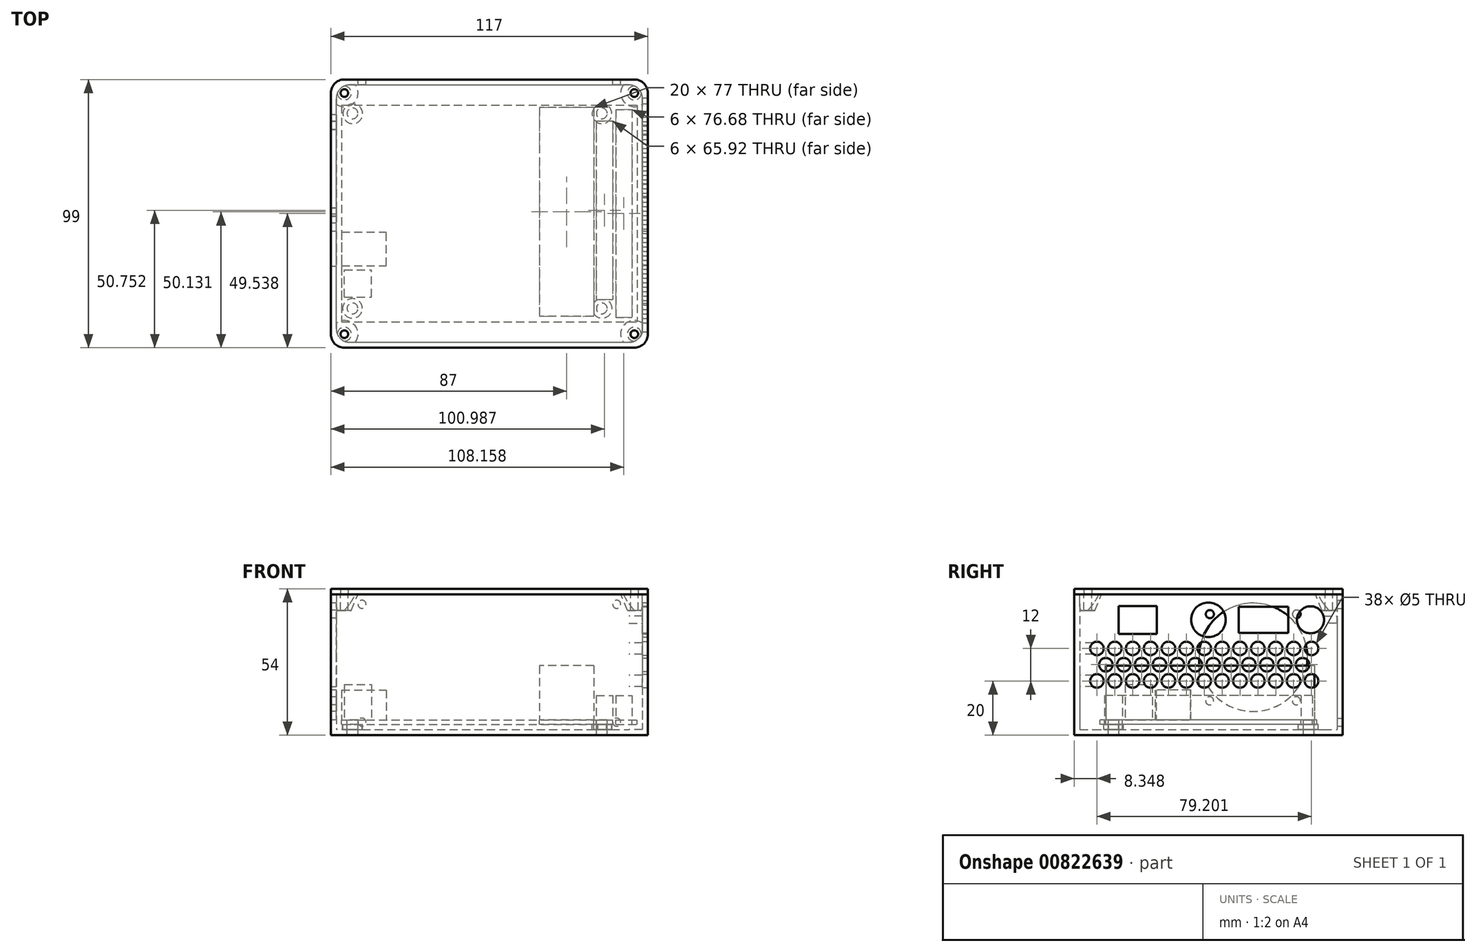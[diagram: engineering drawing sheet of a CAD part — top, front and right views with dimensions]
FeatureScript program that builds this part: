
annotation { "Feature Type Name" : "Feature", "Feature Type Description" : "" }
export const myFeature = defineFeature(function(context is Context, id is Id, definition is map)
    precondition{}
    {
        {
            var Q0;
            Q0=qCreatedBy(makeId("Top.planeOp"),FACE);
            var sketch = newSketch(context, id + "F0", { "sketchPlane" : qUnion([Q0])});
            skLineSegment(sketch, "E0.bottom", {"start": v(-50.5, 37) * mm, "end": v(41.5, 37) * mm, "construction": true});
            skLineSegment(sketch, "E0.top", {"start": v(-50.5, -35) * mm, "end": v(41.5, -35) * mm, "construction": true});
            skLineSegment(sketch, "E0.left", {"start": v(-50.5, 37) * mm, "end": v(-50.5, -35) * mm, "construction": true});
            skLineSegment(sketch, "E0.right", {"start": v(41.5, 37) * mm, "end": v(41.5, -35) * mm, "construction": true});
            skPoint(sketch, "E0.middle", {"position": v(0, 0) * mm});
            skLineSegment(sketch, "E1.bottom", {"start": v(-54.5, 40) * mm, "end": v(54.5, 40) * mm});
            skLineSegment(sketch, "E1.top", {"start": v(-54.5, -40) * mm, "end": v(54.5, -40) * mm});
            skLineSegment(sketch, "E1.left", {"start": v(-54.5, 40) * mm, "end": v(-54.5, -40) * mm});
            skLineSegment(sketch, "E1.right", {"start": v(54.5, 40) * mm, "end": v(54.5, -40) * mm});
            skCircle(sketch, "E2", {"center": v(-50.5, -35) * mm, "radius": 2 * mm});
            skCircle(sketch, "E3", {"center": v(-50.5, 37) * mm, "radius": 2 * mm});
            skCircle(sketch, "E4", {"center": v(41.5, 37) * mm, "radius": 2 * mm});
            skCircle(sketch, "E5", {"center": v(41.5, -35) * mm, "radius": 2 * mm});
            skLineSegment(sketch, "E6.bottom", {"start": v(-53.5, -30.75) * mm, "end": v(-43.5, -30.75) * mm});
            skLineSegment(sketch, "E6.top", {"start": v(-53.5, -20.75) * mm, "end": v(-43.5, -20.75) * mm});
            skLineSegment(sketch, "E6.left", {"start": v(-53.5, -30.75) * mm, "end": v(-53.5, -20.75) * mm});
            skLineSegment(sketch, "E6.right", {"start": v(-43.5, -30.75) * mm, "end": v(-43.5, -20.75) * mm});
            skLineSegment(sketch, "E7.bottom", {"start": v(-54.5, -19.25) * mm, "end": v(-38, -19.25) * mm});
            skLineSegment(sketch, "E7.top", {"start": v(-54.5, -6.75) * mm, "end": v(-38, -6.75) * mm});
            skLineSegment(sketch, "E7.left", {"start": v(-54.5, -19.25) * mm, "end": v(-54.5, -6.75) * mm});
            skLineSegment(sketch, "E7.right", {"start": v(-38, -19.25) * mm, "end": v(-38, -6.75) * mm});
            skLineSegment(sketch, "E8.bottom", {"start": v(38.5, 39.13) * mm, "end": v(18.5, 39.13) * mm});
            skLineSegment(sketch, "E8.top", {"start": v(38.5, -37.87) * mm, "end": v(18.5, -37.87) * mm});
            skLineSegment(sketch, "E8.left", {"start": v(38.5, 39.13) * mm, "end": v(38.5, -37.87) * mm});
            skLineSegment(sketch, "E8.right", {"start": v(18.5, 39.13) * mm, "end": v(18.5, -37.87) * mm});
            skLineSegment(sketch, "E9.bottom", {"start": v(39.49, 34.21) * mm, "end": v(45.49, 34.21) * mm});
            skLineSegment(sketch, "E9.top", {"start": v(39.49, -31.7) * mm, "end": v(45.49, -31.7) * mm});
            skLineSegment(sketch, "E9.left", {"start": v(39.49, 34.21) * mm, "end": v(39.49, -31.7) * mm});
            skLineSegment(sketch, "E9.right", {"start": v(45.49, 34.21) * mm, "end": v(45.49, -31.7) * mm});
            skLineSegment(sketch, "E10.bottom", {"start": v(46.66, 38.38) * mm, "end": v(52.66, 38.38) * mm});
            skLineSegment(sketch, "E10.top", {"start": v(46.66, -38.3) * mm, "end": v(52.66, -38.3) * mm});
            skLineSegment(sketch, "E10.left", {"start": v(46.66, 38.38) * mm, "end": v(46.66, -38.3) * mm});
            skLineSegment(sketch, "E10.right", {"start": v(52.66, 38.38) * mm, "end": v(52.66, -38.3) * mm});
            skSolve(sketch);
        }
        {
            var Q0;
            {var subQ0=sQuery(id+"F0.wireOp",EDGE,"E1.bottom");Q0=makeQuery(id+"F0.imprint","IMPRINT",FACE,{"disambiguationData":[TD([[makeQuery(id+"F0.imprint","IMPRINT",EDGE,{"derivedFrom":subQ0}),-1.0]])]});}
            var Q1;
            Q1=makeQuery(id+"F0.imprint","IMPRINT",FACE,{"disambiguationData":[TD([[makeQuery(id+"F0.imprint","IMPRINT",EDGE,{"derivedFrom":sQuery(id+"F0.wireOp",EDGE,"E7.bottom")}),1.0]])]});
            var Q2;
            Q2=makeQuery(id+"F0.imprint","IMPRINT",FACE,{"disambiguationData":[TD([[makeQuery(id+"F0.imprint","IMPRINT",EDGE,{"derivedFrom":sQuery(id+"F0.wireOp",EDGE,"E6.bottom")}),1.0]])]});
            extrude(context, id + "F1", {"entities" : qUnion([Q0, Q1, Q2]), "oppositeDirection" : true, "depth" : 1.66 * mm, "offsetDistance" : 25 * mm});
        }
        {
            var Q0;
            Q0=makeQuery(id+"F0.imprint","IMPRINT",FACE,{"disambiguationData":[TD([[makeQuery(id+"F0.imprint","IMPRINT",EDGE,{"derivedFrom":sQuery(id+"F0.wireOp",EDGE,"E6.bottom")}),1.0]])]});
            extrude(context, id + "F2", {"entities" : qUnion([Q0]), "operationType" : NewBodyOperationType.ADD, "depth" : 13 * mm, "offsetDistance" : 25 * mm});
        }
        {
            var Q0;
            Q0=makeQuery(id+"F0.imprint","IMPRINT",FACE,{"disambiguationData":[TD([[makeQuery(id+"F0.imprint","IMPRINT",EDGE,{"derivedFrom":sQuery(id+"F0.wireOp",EDGE,"E7.bottom")}),1.0]])]});
            extrude(context, id + "F3", {"entities" : qUnion([Q0]), "operationType" : NewBodyOperationType.ADD, "depth" : 11 * mm, "offsetDistance" : 25 * mm});
        }
        {
            var Q0;
            Q0=makeQuery(id+"F1.opExtrude","CAP_FACE",FACE,{"disambiguationData":[OSD([sQuery(id+"F0.wireOp",EDGE,"E1.bottom"),sQuery(id+"F0.wireOp",EDGE,"E1.top"),sQuery(id+"F0.wireOp",EDGE,"E1.left"),sQuery(id+"F0.wireOp",EDGE,"E1.right"),sQuery(id+"F0.wireOp",EDGE,"E2"),sQuery(id+"F0.wireOp",EDGE,"E3"),sQuery(id+"F0.wireOp",EDGE,"E4"),sQuery(id+"F0.wireOp",EDGE,"E5"),sQuery(id+"F0.wireOp",EDGE,"E7.left")])],"isStart":false});
            var sketch = newSketch(context, id + "F4", { "sketchPlane" : qUnion([Q0])});
            skCircle(sketch, "E11", {"center": v(-50.5, 35) * mm, "radius": 3.62 * mm});
            skCircle(sketch, "E12", {"center": v(41.62, 34.97) * mm, "radius": 3.62 * mm});
            skCircle(sketch, "E13", {"center": v(41.58, -36.84) * mm, "radius": 3.62 * mm});
            skCircle(sketch, "E14", {"center": v(-50.4, -36.84) * mm, "radius": 3.62 * mm});
            skSolve(sketch);
        }
        {
            var Q0;
            Q0=makeQuery(id+"F4.imprint","IMPRINT",FACE,{"disambiguationData":[TD([[makeQuery(id+"F4.imprint","IMPRINT",EDGE,{"derivedFrom":sQuery(id+"F4.wireOp",EDGE,"E11")}),1.0]])]});
            var Q1;
            Q1=makeQuery(id+"F4.imprint","IMPRINT",FACE,{"disambiguationData":[TD([[makeQuery(id+"F4.imprint","IMPRINT",EDGE,{"derivedFrom":sQuery(id+"F4.wireOp",EDGE,"E12")}),1.0]])]});
            var Q2;
            Q2=makeQuery(id+"F4.imprint","IMPRINT",FACE,{"disambiguationData":[TD([[makeQuery(id+"F4.imprint","IMPRINT",EDGE,{"derivedFrom":makeQuery(id+"F1.opExtrude","CAP_EDGE",EDGE,{"disambiguationData":[OSD([sQuery(id+"F0.wireOp",EDGE,"E4")])],"isStart":false})}),1.0]])]});
            var Q3;
            Q3=makeQuery(id+"F4.imprint","IMPRINT",FACE,{"disambiguationData":[TD([[makeQuery(id+"F4.imprint","IMPRINT",EDGE,{"derivedFrom":makeQuery(id+"F1.opExtrude","CAP_EDGE",EDGE,{"disambiguationData":[OSD([sQuery(id+"F0.wireOp",EDGE,"E3")])],"isStart":false})}),1.0]])]});
            var Q4;
            {var subQ0=sQuery(id+"F4.wireOp",EDGE,"E14");var subQ1=makeQuery(id+"F1.opExtrude","CAP_EDGE",EDGE,{"disambiguationData":[OSD([sQuery(id+"F0.wireOp",EDGE,"E1.bottom")])],"isStart":false});var subQ2=makeQuery(id+"F4.imprint","INTERSECT",VERTEX,{"disambiguationData":[OD(0.0)],"derivedFrom":[subQ1,subQ0]});Q4=makeQuery(id+"F4.imprint","IMPRINT",FACE,{"disambiguationData":[TD([[makeQuery(id+"F4.imprint","IMPRINT",EDGE,{"disambiguationData":[TD([[subQ2,-1.0]])],"derivedFrom":subQ0}),1.0]])]});}
            var Q5;
            {var subQ0=sQuery(id+"F4.wireOp",EDGE,"E13");var subQ1=makeQuery(id+"F1.opExtrude","CAP_EDGE",EDGE,{"disambiguationData":[OSD([sQuery(id+"F0.wireOp",EDGE,"E1.bottom")])],"isStart":false});var subQ2=makeQuery(id+"F4.imprint","INTERSECT",VERTEX,{"disambiguationData":[OD(0.0)],"derivedFrom":[subQ1,subQ0]});Q5=makeQuery(id+"F4.imprint","IMPRINT",FACE,{"disambiguationData":[TD([[makeQuery(id+"F4.imprint","IMPRINT",EDGE,{"disambiguationData":[TD([[subQ2,1.0]])],"derivedFrom":subQ0}),1.0]])]});}
            var Q6;
            {var subQ0=sQuery(id+"F4.wireOp",EDGE,"E13");var subQ1=makeQuery(id+"F1.opExtrude","CAP_EDGE",EDGE,{"disambiguationData":[OSD([sQuery(id+"F0.wireOp",EDGE,"E1.bottom")])],"isStart":false});var subQ2=makeQuery(id+"F4.imprint","INTERSECT",VERTEX,{"disambiguationData":[OD(0.0)],"derivedFrom":[subQ1,subQ0]});Q6=makeQuery(id+"F4.imprint","IMPRINT",FACE,{"disambiguationData":[TD([[makeQuery(id+"F4.imprint","IMPRINT",EDGE,{"disambiguationData":[TD([[subQ2,-1.0]])],"derivedFrom":subQ0}),1.0]])]});}
            var Q7;
            {var subQ0=sQuery(id+"F4.wireOp",EDGE,"E13");var subQ1=makeQuery(id+"F1.opExtrude","CAP_EDGE",EDGE,{"disambiguationData":[OSD([sQuery(id+"F0.wireOp",EDGE,"E9.left")])],"isStart":false});var subQ2=makeQuery(id+"F4.imprint","INTERSECT",VERTEX,{"derivedFrom":[subQ1,subQ0]});Q7=makeQuery(id+"F4.imprint","IMPRINT",FACE,{"disambiguationData":[TD([[makeQuery(id+"F4.imprint","IMPRINT",EDGE,{"disambiguationData":[TD([[subQ2,1.0]])],"derivedFrom":subQ0}),1.0]])]});}
            var Q8;
            {var subQ0=sQuery(id+"F4.wireOp",EDGE,"E13");var subQ1=makeQuery(id+"F1.opExtrude","CAP_EDGE",EDGE,{"disambiguationData":[OSD([sQuery(id+"F0.wireOp",EDGE,"E8.left")])],"isStart":false});var subQ2=makeQuery(id+"F4.imprint","INTERSECT",VERTEX,{"disambiguationData":[OD(0.0)],"derivedFrom":[subQ1,subQ0]});Q8=makeQuery(id+"F4.imprint","IMPRINT",FACE,{"disambiguationData":[TD([[makeQuery(id+"F4.imprint","IMPRINT",EDGE,{"disambiguationData":[TD([[subQ2,-1.0]])],"derivedFrom":subQ0}),1.0]])]});}
            var Q9;
            {var subQ0=sQuery(id+"F4.wireOp",EDGE,"E12");var subQ1=makeQuery(id+"F1.opExtrude","CAP_EDGE",EDGE,{"disambiguationData":[OSD([sQuery(id+"F0.wireOp",EDGE,"E8.left")])],"isStart":false});var subQ2=makeQuery(id+"F4.imprint","INTERSECT",VERTEX,{"disambiguationData":[OD(0.0)],"derivedFrom":[subQ1,subQ0]});Q9=makeQuery(id+"F4.imprint","IMPRINT",FACE,{"disambiguationData":[TD([[makeQuery(id+"F4.imprint","IMPRINT",EDGE,{"disambiguationData":[TD([[subQ2,1.0]])],"derivedFrom":subQ0}),1.0]])]});}
            var Q10;
            {var subQ0=sQuery(id+"F4.wireOp",EDGE,"E12");var subQ1=makeQuery(id+"F1.opExtrude","CAP_EDGE",EDGE,{"disambiguationData":[OSD([sQuery(id+"F0.wireOp",EDGE,"E9.top")])],"isStart":false});var subQ2=makeQuery(id+"F4.imprint","INTERSECT",VERTEX,{"disambiguationData":[OD(0.0)],"derivedFrom":[subQ1,subQ0]});Q10=makeQuery(id+"F4.imprint","IMPRINT",FACE,{"disambiguationData":[TD([[makeQuery(id+"F4.imprint","IMPRINT",EDGE,{"disambiguationData":[TD([[subQ2,-1.0]])],"derivedFrom":subQ0}),1.0]])]});}
            var Q11;
            Q11=sQuery(id+"F4.wireOp",EDGE,"E11");
            extrude(context, id + "F5", {"entities" : qUnion([Q0, Q1, Q2, Q3, Q4, Q5, Q6, Q7, Q8, Q9, Q10]), "surfaceEntities" : qUnion([Q11]), "depth" : 2 * mm, "offsetDistance" : 25 * mm});
        }
        {
            var Q0;
            Q0=makeQuery(id+"F5.opExtrude","CAP_FACE",FACE,{"disambiguationData":[OSD([sQuery(id+"F0.wireOp",EDGE,"E2"),sQuery(id+"F4.wireOp",EDGE,"E11")])],"isStart":false});
            var sketch = newSketch(context, id + "F6", { "sketchPlane" : qUnion([Q0])});
            skLineSegment(sketch, "E15.bottom", {"start": v(-56.5, 47.5) * mm, "end": v(56.5, 47.5) * mm});
            skLineSegment(sketch, "E15.top", {"start": v(-56.5, -47.5) * mm, "end": v(56.5, -47.5) * mm});
            skLineSegment(sketch, "E15.left", {"start": v(-56.5, 47.5) * mm, "end": v(-56.5, -47.5) * mm});
            skLineSegment(sketch, "E15.right", {"start": v(56.5, 47.5) * mm, "end": v(56.5, -47.5) * mm});
            skPoint(sketch, "E15.middle", {"position": v(0, 0) * mm});
            skLineSegment(sketch, "E16.bottom", {"start": v(-58.5, 49.5) * mm, "end": v(58.5, 49.5) * mm});
            skLineSegment(sketch, "E16.top", {"start": v(-58.5, -49.5) * mm, "end": v(58.5, -49.5) * mm});
            skLineSegment(sketch, "E16.left", {"start": v(-58.5, 49.5) * mm, "end": v(-58.5, -49.5) * mm});
            skLineSegment(sketch, "E16.right", {"start": v(58.5, 49.5) * mm, "end": v(58.5, -49.5) * mm});
            skCircle(sketch, "E17", {"center": v(-50.5, -37) * mm, "radius": 2 * mm});
            skCircle(sketch, "E18.0.1.0", {"center": v(-50.5, 35) * mm, "radius": 2 * mm});
            skCircle(sketch, "E18.1.0.0", {"center": v(41.5, -37) * mm, "radius": 2 * mm});
            skCircle(sketch, "E18.1.1.0", {"center": v(41.5, 35) * mm, "radius": 2 * mm});
            skLineSegment(sketch, "E18.direction1", {"start": v(-50.5, -37) * mm, "end": v(41.5, -37) * mm, "construction": true});
            skLineSegment(sketch, "E18.direction2", {"start": v(-50.5, -37) * mm, "end": v(-50.5, 35) * mm, "construction": true});
            skSolve(sketch);
        }
        {
            var Q0;
            Q0=makeQuery(id+"F6.imprint","IMPRINT",FACE,{"disambiguationData":[TD([[makeQuery(id+"F6.imprint","IMPRINT",EDGE,{"derivedFrom":sQuery(id+"F6.wireOp",EDGE,"E15.bottom")}),-1.0]])]});
            var Q1;
            Q1=makeQuery(id+"F6.imprint","IMPRINT",FACE,{"disambiguationData":[TD([[makeQuery(id+"F6.imprint","IMPRINT",EDGE,{"derivedFrom":sQuery(id+"F6.wireOp",EDGE,"E15.bottom")}),1.0]])]});
            var Q2;
            Q2=makeQuery(id+"F6.imprint","IMPRINT",FACE,{"disambiguationData":[TD([[makeQuery(id+"F6.imprint","IMPRINT",EDGE,{"derivedFrom":sQuery(id+"F6.wireOp",EDGE,"E18.0.1.0")}),1.0]])]});
            var Q3;
            Q3=sQuery(id+"F6.wireOp",EDGE,"E15.bottom");
            var Q4;
            Q4=sQuery(id+"F6.wireOp",EDGE,"E15.right");
            var Q5;
            Q5=sQuery(id+"F6.wireOp",EDGE,"E15.top");
            var Q6;
            Q6=sQuery(id+"F6.wireOp",EDGE,"E16.left");
            var Q7;
            Q7=sQuery(id+"F6.wireOp",EDGE,"E16.bottom");
            var Q8;
            Q8=sQuery(id+"F6.wireOp",EDGE,"E16.top");
            var Q9;
            Q9=sQuery(id+"F6.wireOp",EDGE,"E16.right");
            extrude(context, id + "F7", {"entities" : qUnion([Q0, Q1, Q2]), "surfaceEntities" : qUnion([Q3, Q4, Q5, Q6, Q7, Q8, Q9]), "depth" : 2 * mm, "offsetDistance" : 25 * mm});
        }
        {
            var Q0;
            Q0=makeQuery(id+"F6.imprint","IMPRINT",FACE,{"disambiguationData":[TD([[makeQuery(id+"F6.imprint","IMPRINT",EDGE,{"derivedFrom":sQuery(id+"F6.wireOp",EDGE,"E15.bottom")}),1.0]])]});
            extrude(context, id + "F8", {"entities" : qUnion([Q0]), "operationType" : NewBodyOperationType.ADD, "oppositeDirection" : true, "depth" : 50 * mm, "offsetDistance" : 25 * mm});
        }
        {
            var Q0;
            {var subQ0=sQuery(id+"F6.wireOp",EDGE,"E16.left");Q0=makeQuery(id+"F8.boolean.opBoolean","MERGE",FACE,{"derivedFrom":[makeQuery(id+"F7.opExtrude","SWEPT_FACE",FACE,{"disambiguationData":[OSD([subQ0])]}),makeQuery(id+"F8.opExtrude","SWEPT_FACE",FACE,{"disambiguationData":[OSD([subQ0])]})]});}
            var sketch = newSketch(context, id + "F9", { "sketchPlane" : qUnion([Q0])});
            skLineSegment(sketch, "E19.bottom", {"start": v(6.53, 0) * mm, "end": v(19.53, 0) * mm});
            skLineSegment(sketch, "E19.top", {"start": v(6.53, 11) * mm, "end": v(19.53, 11) * mm});
            skLineSegment(sketch, "E19.left", {"start": v(6.53, 0) * mm, "end": v(6.53, 11) * mm});
            skLineSegment(sketch, "E19.right", {"start": v(19.53, 0) * mm, "end": v(19.53, 11) * mm});
            skSolve(sketch);
        }
        {
            var Q0;
            Q0 = qSketchRegion(id + "F9", true);
            extrude(context, id + "F10", {"entities" : qUnion([Q0]), "operationType" : NewBodyOperationType.REMOVE, "oppositeDirection" : true, "depth" : 2 * mm, "offsetDistance" : 25 * mm});
        }
        {
            var Q0;
            {var subQ0=sQuery(id+"F6.wireOp",EDGE,"E16.top");Q0=makeQuery(id+"F8.boolean.opBoolean","MERGE",FACE,{"derivedFrom":[makeQuery(id+"F7.opExtrude","SWEPT_FACE",FACE,{"disambiguationData":[OSD([subQ0])]}),makeQuery(id+"F8.opExtrude","SWEPT_FACE",FACE,{"disambiguationData":[OSD([subQ0])]})]});}
            var sketch = newSketch(context, id + "F11", { "sketchPlane" : qUnion([Q0])});
            skLineSegment(sketch, "E20.bottom", {"start": v(-47, -0.86) * mm, "end": v(47, -0.86) * mm, "construction": true});
            skLineSegment(sketch, "E20.top", {"start": v(-47, 42.64) * mm, "end": v(47, 42.64) * mm, "construction": true});
            skLineSegment(sketch, "E20.left", {"start": v(-47, -0.86) * mm, "end": v(-47, 42.64) * mm, "construction": true});
            skLineSegment(sketch, "E20.right", {"start": v(47, -0.86) * mm, "end": v(47, 42.64) * mm, "construction": true});
            skCircle(sketch, "E21", {"center": v(-47, 42.64) * mm, "radius": 1.5 * mm});
            skCircle(sketch, "E22", {"center": v(47, 42.64) * mm, "radius": 1.5 * mm});
            skCircle(sketch, "E23", {"center": v(47, -0.86) * mm, "radius": 1.5 * mm});
            skCircle(sketch, "E24", {"center": v(-47, -0.86) * mm, "radius": 1.5 * mm});
            skSolve(sketch);
        }
        {
            var Q0;
            Q0 = qSketchRegion(id + "F11", true);
            extrude(context, id + "F12", {"entities" : qUnion([Q0]), "operationType" : NewBodyOperationType.REMOVE, "oppositeDirection" : true, "depth" : 2 * mm, "offsetDistance" : 25 * mm});
        }
        {
            var Q0;
            {var subQ0=sQuery(id+"F6.wireOp",EDGE,"E16.right");Q0=makeQuery(id+"F8.boolean.opBoolean","MERGE",FACE,{"derivedFrom":[makeQuery(id+"F7.opExtrude","SWEPT_FACE",FACE,{"disambiguationData":[OSD([subQ0])]}),makeQuery(id+"F8.opExtrude","SWEPT_FACE",FACE,{"disambiguationData":[OSD([subQ0])]})]});}
            var sketch = newSketch(context, id + "F13", { "sketchPlane" : qUnion([Q0])});
            skLineSegment(sketch, "E25.bottom", {"start": v(-33.1, 31.75) * mm, "end": v(-19.1, 31.75) * mm});
            skLineSegment(sketch, "E25.top", {"start": v(-33.1, 42) * mm, "end": v(-19.1, 42) * mm});
            skLineSegment(sketch, "E25.left", {"start": v(-33.1, 31.75) * mm, "end": v(-33.1, 42) * mm});
            skLineSegment(sketch, "E25.right", {"start": v(-19.1, 31.75) * mm, "end": v(-19.1, 42) * mm});
            skCircle(sketch, "E26", {"center": v(-41.15, 26.34) * mm, "radius": 2.5 * mm});
            skCircle(sketch, "E27.1.0.0", {"center": v(-34.55, 26.34) * mm, "radius": 2.5 * mm});
            skCircle(sketch, "E27.2.0.0", {"center": v(-27.95, 26.34) * mm, "radius": 2.5 * mm});
            skCircle(sketch, "E27.3.0.0", {"center": v(-21.35, 26.34) * mm, "radius": 2.5 * mm});
            skCircle(sketch, "E27.4.0.0", {"center": v(-14.75, 26.34) * mm, "radius": 2.5 * mm});
            skCircle(sketch, "E27.5.0.0", {"center": v(-8.15, 26.34) * mm, "radius": 2.5 * mm});
            skCircle(sketch, "E27.6.0.0", {"center": v(-1.55, 26.34) * mm, "radius": 2.5 * mm});
            skCircle(sketch, "E27.7.0.0", {"center": v(5.05, 26.34) * mm, "radius": 2.5 * mm});
            skCircle(sketch, "E27.8.0.0", {"center": v(11.65, 26.34) * mm, "radius": 2.5 * mm});
            skCircle(sketch, "E27.9.0.0", {"center": v(18.25, 26.34) * mm, "radius": 2.5 * mm});
            skCircle(sketch, "E27.10.0.0", {"center": v(24.85, 26.34) * mm, "radius": 2.5 * mm});
            skCircle(sketch, "E27.11.0.0", {"center": v(31.45, 26.34) * mm, "radius": 2.5 * mm});
            skCircle(sketch, "E27.12.0.0", {"center": v(38.05, 26.34) * mm, "radius": 2.5 * mm});
            skLineSegment(sketch, "E27.direction1", {"start": v(-41.15, 26.34) * mm, "end": v(-34.55, 26.34) * mm, "construction": true});
            skCircle(sketch, "E28", {"center": v(-37.85, 20.34) * mm, "radius": 2.5 * mm});
            skPoint(sketch, "E28.centerSnap0", {"position": v(-37.85, 26.34) * mm});
            skCircle(sketch, "E29.1.0.0", {"center": v(-31.25, 20.34) * mm, "radius": 2.5 * mm});
            skCircle(sketch, "E29.2.0.0", {"center": v(-24.65, 20.34) * mm, "radius": 2.5 * mm});
            skCircle(sketch, "E29.3.0.0", {"center": v(-18.05, 20.34) * mm, "radius": 2.5 * mm});
            skCircle(sketch, "E29.4.0.0", {"center": v(-11.45, 20.34) * mm, "radius": 2.5 * mm});
            skCircle(sketch, "E29.5.0.0", {"center": v(-4.85, 20.34) * mm, "radius": 2.5 * mm});
            skCircle(sketch, "E29.6.0.0", {"center": v(1.75, 20.34) * mm, "radius": 2.5 * mm});
            skCircle(sketch, "E29.7.0.0", {"center": v(8.35, 20.34) * mm, "radius": 2.5 * mm});
            skCircle(sketch, "E29.8.0.0", {"center": v(14.95, 20.34) * mm, "radius": 2.5 * mm});
            skCircle(sketch, "E29.9.0.0", {"center": v(21.55, 20.34) * mm, "radius": 2.5 * mm});
            skCircle(sketch, "E29.10.0.0", {"center": v(28.15, 20.34) * mm, "radius": 2.5 * mm});
            skCircle(sketch, "E29.11.0.0", {"center": v(34.75, 20.34) * mm, "radius": 2.5 * mm});
            skLineSegment(sketch, "E29.direction1", {"start": v(-37.85, 20.34) * mm, "end": v(-31.25, 20.34) * mm, "construction": true});
            skCircle(sketch, "E30.1.0.0", {"center": v(-27.95, 14.34) * mm, "radius": 2.5 * mm});
            skPoint(sketch, "E30.1.0.1", {"position": v(-37.85, 14.34) * mm});
            skCircle(sketch, "E30.1.0.2", {"center": v(-8.15, 14.34) * mm, "radius": 2.5 * mm});
            skCircle(sketch, "E30.1.0.3", {"center": v(-1.55, 14.34) * mm, "radius": 2.5 * mm});
            skCircle(sketch, "E30.1.0.4", {"center": v(-21.35, 14.34) * mm, "radius": 2.5 * mm});
            skCircle(sketch, "E30.1.0.5", {"center": v(-14.75, 14.34) * mm, "radius": 2.5 * mm});
            skCircle(sketch, "E30.1.0.6", {"center": v(5.05, 14.34) * mm, "radius": 2.5 * mm});
            skCircle(sketch, "E30.1.0.7", {"center": v(11.65, 14.34) * mm, "radius": 2.5 * mm});
            skLineSegment(sketch, "E30.1.0.8", {"start": v(-41.15, 14.34) * mm, "end": v(-34.55, 14.34) * mm, "construction": true});
            skCircle(sketch, "E30.1.0.9", {"center": v(38.05, 14.34) * mm, "radius": 2.5 * mm});
            skCircle(sketch, "E30.1.0.10", {"center": v(18.25, 14.34) * mm, "radius": 2.5 * mm});
            skCircle(sketch, "E30.1.0.11", {"center": v(24.85, 14.34) * mm, "radius": 2.5 * mm});
            skCircle(sketch, "E30.1.0.12", {"center": v(31.45, 14.34) * mm, "radius": 2.5 * mm});
            skCircle(sketch, "E30.1.0.13", {"center": v(-41.15, 14.34) * mm, "radius": 2.5 * mm});
            skCircle(sketch, "E30.1.0.14", {"center": v(-34.55, 14.34) * mm, "radius": 2.5 * mm});
            skLineSegment(sketch, "E30.direction1", {"start": v(-41.15, 26.34) * mm, "end": v(-41.15, 14.34) * mm, "construction": true});
            skLineSegment(sketch, "E31.direction1", {"start": v(-37.85, 20.34) * mm, "end": v(-37.96, 8.34) * mm, "construction": true});
            skCircle(sketch, "E32", {"center": v(0, 36.91) * mm, "radius": 6.38 * mm});
            skPoint(sketch, "E32.centerSnap0", {"position": v(-19.1, 36.88) * mm});
            skCircle(sketch, "E33", {"center": v(37.68, 36.91) * mm, "radius": 5 * mm});
            skLineSegment(sketch, "E34.bottom", {"start": v(29.44, 41.75) * mm, "end": v(11.13, 41.75) * mm});
            skLineSegment(sketch, "E34.top", {"start": v(29.44, 32.08) * mm, "end": v(11.13, 32.08) * mm});
            skLineSegment(sketch, "E34.left", {"start": v(29.44, 41.75) * mm, "end": v(29.44, 32.08) * mm});
            skLineSegment(sketch, "E34.right", {"start": v(11.13, 41.75) * mm, "end": v(11.13, 32.08) * mm});
            skPoint(sketch, "E34.middle", {"position": v(20.28, 36.91) * mm});
            skLineSegment(sketch, "E35", {"start": v(37.68, 36.91) * mm, "end": v(-34.66, 36.91) * mm, "construction": true});
            skSolve(sketch);
        }
        {
            var Q0;
            Q0=makeQuery(id+"F13.imprint","IMPRINT",FACE,{"disambiguationData":[TD([[makeQuery(id+"F13.imprint","IMPRINT",EDGE,{"derivedFrom":sQuery(id+"F13.wireOp",EDGE,"E25.bottom")}),1.0]])]});
            var Q1;
            Q1=makeQuery(id+"F13.imprint","IMPRINT",FACE,{"disambiguationData":[TD([[makeQuery(id+"F13.imprint","IMPRINT",EDGE,{"derivedFrom":sQuery(id+"F13.wireOp",EDGE,"E32")}),1.0]])]});
            var Q2;
            Q2=makeQuery(id+"F13.imprint","IMPRINT",FACE,{"disambiguationData":[TD([[makeQuery(id+"F13.imprint","IMPRINT",EDGE,{"derivedFrom":sQuery(id+"F13.wireOp",EDGE,"E34.bottom")}),1.0]])]});
            var Q3;
            Q3=makeQuery(id+"F13.imprint","IMPRINT",FACE,{"disambiguationData":[TD([[makeQuery(id+"F13.imprint","IMPRINT",EDGE,{"derivedFrom":sQuery(id+"F13.wireOp",EDGE,"E33")}),1.0]])]});
            var Q4;
            Q4=makeQuery(id+"F8.opExtrude","SWEPT_FACE",FACE,{"disambiguationData":[OSD([sQuery(id+"F6.wireOp",EDGE,"E15.right")])]});
            extrude(context, id + "F14", {"entities" : qUnion([Q0, Q1, Q2, Q3]), "operationType" : NewBodyOperationType.REMOVE, "endBound" : BoundingType.UP_TO_SURFACE, "oppositeDirection" : true, "depth" : 2.5 * mm, "endBoundEntityFace" : qUnion([Q4]), "offsetDistance" : 25 * mm});
        }
        {
            var Q0;
            Q0=makeQuery(id+"F9.imprint","IMPRINT",FACE,{"disambiguationData":[TD([[makeQuery(id+"F9.imprint","IMPRINT",EDGE,{"derivedFrom":sQuery(id+"F9.wireOp",EDGE,"E19.bottom")}),-1.0]])]});
            var sketch = newSketch(context, id + "F15", { "sketchPlane" : qUnion([Q0])});
            skLineSegment(sketch, "E36.bottom", {"start": v(-36.53, 43.01) * mm, "end": v(3.47, 43.01) * mm, "construction": true});
            skLineSegment(sketch, "E36.top", {"start": v(-36.53, 3.16) * mm, "end": v(3.47, 3.16) * mm, "construction": true});
            skLineSegment(sketch, "E36.left", {"start": v(-36.53, 43) * mm, "end": v(-36.53, 3.16) * mm, "construction": true});
            skLineSegment(sketch, "E36.right", {"start": v(3.47, 43) * mm, "end": v(3.47, 3.16) * mm, "construction": true});
            skArc(sketch, "E37", {"start": v(3.47, 23.09) * mm, "mid": v(-35.69, 28.83) * mm, "end": v(0.17, 12.08) * mm});
            skPoint(sketch, "E37.centerSnap0", {"position": v(-36.53, 23.08) * mm});
            skPoint(sketch, "E37.centerSnap1", {"position": v(-16.53, 43.01) * mm});
            skLineSegment(sketch, "E38.bottom", {"start": v(3.47, 12.09) * mm, "end": v(0.17, 12.09) * mm});
            skCircle(sketch, "E39", {"center": v(-32.53, 39.01) * mm, "radius": 1.5 * mm});
            skCircle(sketch, "E40", {"center": v(-0.53, 39.01) * mm, "radius": 1.5 * mm});
            skLineSegment(sketch, "E41", {"start": v(-32.53, 39.01) * mm, "end": v(-0.53, 39.01) * mm, "construction": true});
            skCircle(sketch, "E42.1.0.0", {"center": v(-32.44, 7.01) * mm, "radius": 1.5 * mm});
            skCircle(sketch, "E42.1.0.1", {"center": v(-0.44, 7.01) * mm, "radius": 1.5 * mm});
            skLineSegment(sketch, "E42.direction1", {"start": v(-32.53, 39.01) * mm, "end": v(-32.44, 7.01) * mm, "construction": true});
            skLineSegment(sketch, "E43", {"start": v(3.47, 23.09) * mm, "end": v(3.47, 12.08) * mm});
            skLineSegment(sketch, "E44", {"start": v(-0.53, 39.01) * mm, "end": v(-0.44, 7.01) * mm, "construction": true});
            skLineSegment(sketch, "E45", {"start": v(-0.44, 7.01) * mm, "end": v(-32.44, 7.01) * mm, "construction": true});
            skSolve(sketch);
        }
        {
            var Q0;
            Q0=makeQuery(id+"F13.imprint","IMPRINT",FACE,{"disambiguationData":[TD([[makeQuery(id+"F13.imprint","IMPRINT",EDGE,{"derivedFrom":sQuery(id+"F13.wireOp",EDGE,"E26")}),1.0]])]});
            var Q1;
            Q1=makeQuery(id+"F13.imprint","IMPRINT",FACE,{"disambiguationData":[TD([[makeQuery(id+"F13.imprint","IMPRINT",EDGE,{"derivedFrom":sQuery(id+"F13.wireOp",EDGE,"E27.1.0.0")}),1.0]])]});
            var Q2;
            Q2=makeQuery(id+"F13.imprint","IMPRINT",FACE,{"disambiguationData":[TD([[makeQuery(id+"F13.imprint","IMPRINT",EDGE,{"derivedFrom":sQuery(id+"F13.wireOp",EDGE,"E27.2.0.0")}),1.0]])]});
            var Q3;
            Q3=makeQuery(id+"F13.imprint","IMPRINT",FACE,{"disambiguationData":[TD([[makeQuery(id+"F13.imprint","IMPRINT",EDGE,{"derivedFrom":sQuery(id+"F13.wireOp",EDGE,"E27.3.0.0")}),1.0]])]});
            var Q4;
            Q4=makeQuery(id+"F13.imprint","IMPRINT",FACE,{"disambiguationData":[TD([[makeQuery(id+"F13.imprint","IMPRINT",EDGE,{"derivedFrom":sQuery(id+"F13.wireOp",EDGE,"E27.4.0.0")}),1.0]])]});
            var Q5;
            Q5=makeQuery(id+"F13.imprint","IMPRINT",FACE,{"disambiguationData":[TD([[makeQuery(id+"F13.imprint","IMPRINT",EDGE,{"derivedFrom":sQuery(id+"F13.wireOp",EDGE,"E27.5.0.0")}),1.0]])]});
            var Q6;
            Q6=makeQuery(id+"F13.imprint","IMPRINT",FACE,{"disambiguationData":[TD([[makeQuery(id+"F13.imprint","IMPRINT",EDGE,{"derivedFrom":sQuery(id+"F13.wireOp",EDGE,"E27.6.0.0")}),1.0]])]});
            var Q7;
            Q7=makeQuery(id+"F13.imprint","IMPRINT",FACE,{"disambiguationData":[TD([[makeQuery(id+"F13.imprint","IMPRINT",EDGE,{"derivedFrom":sQuery(id+"F13.wireOp",EDGE,"E27.7.0.0")}),1.0]])]});
            var Q8;
            Q8=makeQuery(id+"F13.imprint","IMPRINT",FACE,{"disambiguationData":[TD([[makeQuery(id+"F13.imprint","IMPRINT",EDGE,{"derivedFrom":sQuery(id+"F13.wireOp",EDGE,"E27.8.0.0")}),1.0]])]});
            var Q9;
            Q9=makeQuery(id+"F13.imprint","IMPRINT",FACE,{"disambiguationData":[TD([[makeQuery(id+"F13.imprint","IMPRINT",EDGE,{"derivedFrom":sQuery(id+"F13.wireOp",EDGE,"E27.9.0.0")}),1.0]])]});
            var Q10;
            Q10=makeQuery(id+"F13.imprint","IMPRINT",FACE,{"disambiguationData":[TD([[makeQuery(id+"F13.imprint","IMPRINT",EDGE,{"derivedFrom":sQuery(id+"F13.wireOp",EDGE,"E27.10.0.0")}),1.0]])]});
            var Q11;
            Q11=makeQuery(id+"F13.imprint","IMPRINT",FACE,{"disambiguationData":[TD([[makeQuery(id+"F13.imprint","IMPRINT",EDGE,{"derivedFrom":sQuery(id+"F13.wireOp",EDGE,"E27.11.0.0")}),1.0]])]});
            var Q12;
            Q12=makeQuery(id+"F13.imprint","IMPRINT",FACE,{"disambiguationData":[TD([[makeQuery(id+"F13.imprint","IMPRINT",EDGE,{"derivedFrom":sQuery(id+"F13.wireOp",EDGE,"E27.12.0.0")}),1.0]])]});
            var Q13;
            Q13=makeQuery(id+"F13.imprint","IMPRINT",FACE,{"disambiguationData":[TD([[makeQuery(id+"F13.imprint","IMPRINT",EDGE,{"derivedFrom":sQuery(id+"F13.wireOp",EDGE,"E29.11.0.0")}),1.0]])]});
            var Q14;
            Q14=makeQuery(id+"F13.imprint","IMPRINT",FACE,{"disambiguationData":[TD([[makeQuery(id+"F13.imprint","IMPRINT",EDGE,{"derivedFrom":sQuery(id+"F13.wireOp",EDGE,"E29.10.0.0")}),1.0]])]});
            var Q15;
            Q15=makeQuery(id+"F13.imprint","IMPRINT",FACE,{"disambiguationData":[TD([[makeQuery(id+"F13.imprint","IMPRINT",EDGE,{"derivedFrom":sQuery(id+"F13.wireOp",EDGE,"E29.9.0.0")}),1.0]])]});
            var Q16;
            Q16=makeQuery(id+"F13.imprint","IMPRINT",FACE,{"disambiguationData":[TD([[makeQuery(id+"F13.imprint","IMPRINT",EDGE,{"derivedFrom":sQuery(id+"F13.wireOp",EDGE,"E29.8.0.0")}),1.0]])]});
            var Q17;
            Q17=makeQuery(id+"F13.imprint","IMPRINT",FACE,{"disambiguationData":[TD([[makeQuery(id+"F13.imprint","IMPRINT",EDGE,{"derivedFrom":sQuery(id+"F13.wireOp",EDGE,"E29.7.0.0")}),1.0]])]});
            var Q18;
            Q18=makeQuery(id+"F13.imprint","IMPRINT",FACE,{"disambiguationData":[TD([[makeQuery(id+"F13.imprint","IMPRINT",EDGE,{"derivedFrom":sQuery(id+"F13.wireOp",EDGE,"E29.6.0.0")}),1.0]])]});
            var Q19;
            Q19=makeQuery(id+"F13.imprint","IMPRINT",FACE,{"disambiguationData":[TD([[makeQuery(id+"F13.imprint","IMPRINT",EDGE,{"derivedFrom":sQuery(id+"F13.wireOp",EDGE,"E29.5.0.0")}),1.0]])]});
            var Q20;
            Q20=makeQuery(id+"F13.imprint","IMPRINT",FACE,{"disambiguationData":[TD([[makeQuery(id+"F13.imprint","IMPRINT",EDGE,{"derivedFrom":sQuery(id+"F13.wireOp",EDGE,"E29.4.0.0")}),1.0]])]});
            var Q21;
            Q21=makeQuery(id+"F13.imprint","IMPRINT",FACE,{"disambiguationData":[TD([[makeQuery(id+"F13.imprint","IMPRINT",EDGE,{"derivedFrom":sQuery(id+"F13.wireOp",EDGE,"E29.3.0.0")}),1.0]])]});
            var Q22;
            Q22=makeQuery(id+"F13.imprint","IMPRINT",FACE,{"disambiguationData":[TD([[makeQuery(id+"F13.imprint","IMPRINT",EDGE,{"derivedFrom":sQuery(id+"F13.wireOp",EDGE,"E29.2.0.0")}),1.0]])]});
            var Q23;
            Q23=makeQuery(id+"F13.imprint","IMPRINT",FACE,{"disambiguationData":[TD([[makeQuery(id+"F13.imprint","IMPRINT",EDGE,{"derivedFrom":sQuery(id+"F13.wireOp",EDGE,"E29.1.0.0")}),1.0]])]});
            var Q24;
            Q24=makeQuery(id+"F13.imprint","IMPRINT",FACE,{"disambiguationData":[TD([[makeQuery(id+"F13.imprint","IMPRINT",EDGE,{"derivedFrom":sQuery(id+"F13.wireOp",EDGE,"E28")}),1.0]])]});
            var Q25;
            Q25=makeQuery(id+"F13.imprint","IMPRINT",FACE,{"disambiguationData":[TD([[makeQuery(id+"F13.imprint","IMPRINT",EDGE,{"derivedFrom":sQuery(id+"F13.wireOp",EDGE,"E30.1.0.13")}),1.0]])]});
            var Q26;
            Q26=makeQuery(id+"F13.imprint","IMPRINT",FACE,{"disambiguationData":[TD([[makeQuery(id+"F13.imprint","IMPRINT",EDGE,{"derivedFrom":sQuery(id+"F13.wireOp",EDGE,"E30.1.0.14")}),1.0]])]});
            var Q27;
            Q27=makeQuery(id+"F13.imprint","IMPRINT",FACE,{"disambiguationData":[TD([[makeQuery(id+"F13.imprint","IMPRINT",EDGE,{"derivedFrom":sQuery(id+"F13.wireOp",EDGE,"E30.1.0.0")}),1.0]])]});
            var Q28;
            Q28=makeQuery(id+"F13.imprint","IMPRINT",FACE,{"disambiguationData":[TD([[makeQuery(id+"F13.imprint","IMPRINT",EDGE,{"derivedFrom":sQuery(id+"F13.wireOp",EDGE,"E30.1.0.4")}),1.0]])]});
            var Q29;
            Q29=makeQuery(id+"F13.imprint","IMPRINT",FACE,{"disambiguationData":[TD([[makeQuery(id+"F13.imprint","IMPRINT",EDGE,{"derivedFrom":sQuery(id+"F13.wireOp",EDGE,"E30.1.0.5")}),1.0]])]});
            var Q30;
            Q30=makeQuery(id+"F13.imprint","IMPRINT",FACE,{"disambiguationData":[TD([[makeQuery(id+"F13.imprint","IMPRINT",EDGE,{"derivedFrom":sQuery(id+"F13.wireOp",EDGE,"E30.1.0.2")}),1.0]])]});
            var Q31;
            Q31=makeQuery(id+"F13.imprint","IMPRINT",FACE,{"disambiguationData":[TD([[makeQuery(id+"F13.imprint","IMPRINT",EDGE,{"derivedFrom":sQuery(id+"F13.wireOp",EDGE,"E30.1.0.3")}),1.0]])]});
            var Q32;
            Q32=makeQuery(id+"F13.imprint","IMPRINT",FACE,{"disambiguationData":[TD([[makeQuery(id+"F13.imprint","IMPRINT",EDGE,{"derivedFrom":sQuery(id+"F13.wireOp",EDGE,"E30.1.0.6")}),1.0]])]});
            var Q33;
            Q33=makeQuery(id+"F13.imprint","IMPRINT",FACE,{"disambiguationData":[TD([[makeQuery(id+"F13.imprint","IMPRINT",EDGE,{"derivedFrom":sQuery(id+"F13.wireOp",EDGE,"E30.1.0.7")}),1.0]])]});
            var Q34;
            Q34=makeQuery(id+"F13.imprint","IMPRINT",FACE,{"disambiguationData":[TD([[makeQuery(id+"F13.imprint","IMPRINT",EDGE,{"derivedFrom":sQuery(id+"F13.wireOp",EDGE,"E30.1.0.10")}),1.0]])]});
            var Q35;
            Q35=makeQuery(id+"F13.imprint","IMPRINT",FACE,{"disambiguationData":[TD([[makeQuery(id+"F13.imprint","IMPRINT",EDGE,{"derivedFrom":sQuery(id+"F13.wireOp",EDGE,"E30.1.0.11")}),1.0]])]});
            var Q36;
            Q36=makeQuery(id+"F13.imprint","IMPRINT",FACE,{"disambiguationData":[TD([[makeQuery(id+"F13.imprint","IMPRINT",EDGE,{"derivedFrom":sQuery(id+"F13.wireOp",EDGE,"E30.1.0.12")}),1.0]])]});
            var Q37;
            Q37=makeQuery(id+"F13.imprint","IMPRINT",FACE,{"disambiguationData":[TD([[makeQuery(id+"F13.imprint","IMPRINT",EDGE,{"derivedFrom":sQuery(id+"F13.wireOp",EDGE,"E30.1.0.9")}),1.0]])]});
            var Q38;
            Q38=makeQuery(id+"F13.imprint","IMPRINT",FACE,{"disambiguationData":[TD([[makeQuery(id+"F13.imprint","IMPRINT",EDGE,{"derivedFrom":sQuery(id+"F13.wireOp",EDGE,"E31.1.0.11")}),1.0]])]});
            var Q39;
            Q39=makeQuery(id+"F13.imprint","IMPRINT",FACE,{"disambiguationData":[TD([[makeQuery(id+"F13.imprint","IMPRINT",EDGE,{"derivedFrom":sQuery(id+"F13.wireOp",EDGE,"E31.1.0.10")}),1.0]])]});
            var Q40;
            Q40=makeQuery(id+"F13.imprint","IMPRINT",FACE,{"disambiguationData":[TD([[makeQuery(id+"F13.imprint","IMPRINT",EDGE,{"derivedFrom":sQuery(id+"F13.wireOp",EDGE,"E31.1.0.9")}),1.0]])]});
            var Q41;
            Q41=makeQuery(id+"F13.imprint","IMPRINT",FACE,{"disambiguationData":[TD([[makeQuery(id+"F13.imprint","IMPRINT",EDGE,{"derivedFrom":sQuery(id+"F13.wireOp",EDGE,"E31.1.0.8")}),1.0]])]});
            var Q42;
            Q42=makeQuery(id+"F13.imprint","IMPRINT",FACE,{"disambiguationData":[TD([[makeQuery(id+"F13.imprint","IMPRINT",EDGE,{"derivedFrom":sQuery(id+"F13.wireOp",EDGE,"E31.1.0.7")}),1.0]])]});
            var Q43;
            Q43=makeQuery(id+"F13.imprint","IMPRINT",FACE,{"disambiguationData":[TD([[makeQuery(id+"F13.imprint","IMPRINT",EDGE,{"derivedFrom":sQuery(id+"F13.wireOp",EDGE,"E31.1.0.6")}),1.0]])]});
            var Q44;
            Q44=makeQuery(id+"F13.imprint","IMPRINT",FACE,{"disambiguationData":[TD([[makeQuery(id+"F13.imprint","IMPRINT",EDGE,{"derivedFrom":sQuery(id+"F13.wireOp",EDGE,"E31.1.0.5")}),1.0]])]});
            var Q45;
            Q45=makeQuery(id+"F13.imprint","IMPRINT",FACE,{"disambiguationData":[TD([[makeQuery(id+"F13.imprint","IMPRINT",EDGE,{"derivedFrom":sQuery(id+"F13.wireOp",EDGE,"E31.1.0.4")}),1.0]])]});
            var Q46;
            Q46=makeQuery(id+"F13.imprint","IMPRINT",FACE,{"disambiguationData":[TD([[makeQuery(id+"F13.imprint","IMPRINT",EDGE,{"derivedFrom":sQuery(id+"F13.wireOp",EDGE,"E31.1.0.3")}),1.0]])]});
            var Q47;
            Q47=makeQuery(id+"F13.imprint","IMPRINT",FACE,{"disambiguationData":[TD([[makeQuery(id+"F13.imprint","IMPRINT",EDGE,{"derivedFrom":sQuery(id+"F13.wireOp",EDGE,"E31.1.0.2")}),1.0]])]});
            var Q48;
            Q48=makeQuery(id+"F13.imprint","IMPRINT",FACE,{"disambiguationData":[TD([[makeQuery(id+"F13.imprint","IMPRINT",EDGE,{"derivedFrom":sQuery(id+"F13.wireOp",EDGE,"E31.1.0.1")}),1.0]])]});
            var Q49;
            Q49=makeQuery(id+"F13.imprint","IMPRINT",FACE,{"disambiguationData":[TD([[makeQuery(id+"F13.imprint","IMPRINT",EDGE,{"derivedFrom":sQuery(id+"F13.wireOp",EDGE,"E31.1.0.0")}),1.0]])]});
            var Q50;
            Q50=makeQuery(id+"F13.imprint","IMPRINT",FACE,{"disambiguationData":[TD([[makeQuery(id+"F13.imprint","IMPRINT",EDGE,{"derivedFrom":sQuery(id+"F13.wireOp",EDGE,"E30.2.0.13")}),1.0]])]});
            var Q51;
            Q51=makeQuery(id+"F13.imprint","IMPRINT",FACE,{"disambiguationData":[TD([[makeQuery(id+"F13.imprint","IMPRINT",EDGE,{"derivedFrom":sQuery(id+"F13.wireOp",EDGE,"E30.2.0.14")}),1.0]])]});
            var Q52;
            Q52=makeQuery(id+"F13.imprint","IMPRINT",FACE,{"disambiguationData":[TD([[makeQuery(id+"F13.imprint","IMPRINT",EDGE,{"derivedFrom":sQuery(id+"F13.wireOp",EDGE,"E30.2.0.0")}),1.0]])]});
            var Q53;
            Q53=makeQuery(id+"F13.imprint","IMPRINT",FACE,{"disambiguationData":[TD([[makeQuery(id+"F13.imprint","IMPRINT",EDGE,{"derivedFrom":sQuery(id+"F13.wireOp",EDGE,"E30.2.0.4")}),1.0]])]});
            var Q54;
            Q54=makeQuery(id+"F13.imprint","IMPRINT",FACE,{"disambiguationData":[TD([[makeQuery(id+"F13.imprint","IMPRINT",EDGE,{"derivedFrom":sQuery(id+"F13.wireOp",EDGE,"E30.2.0.5")}),1.0]])]});
            var Q55;
            Q55=makeQuery(id+"F13.imprint","IMPRINT",FACE,{"disambiguationData":[TD([[makeQuery(id+"F13.imprint","IMPRINT",EDGE,{"derivedFrom":sQuery(id+"F13.wireOp",EDGE,"E30.2.0.2")}),1.0]])]});
            var Q56;
            Q56=makeQuery(id+"F13.imprint","IMPRINT",FACE,{"disambiguationData":[TD([[makeQuery(id+"F13.imprint","IMPRINT",EDGE,{"derivedFrom":sQuery(id+"F13.wireOp",EDGE,"E30.2.0.3")}),1.0]])]});
            var Q57;
            Q57=makeQuery(id+"F13.imprint","IMPRINT",FACE,{"disambiguationData":[TD([[makeQuery(id+"F13.imprint","IMPRINT",EDGE,{"derivedFrom":sQuery(id+"F13.wireOp",EDGE,"E30.2.0.6")}),1.0]])]});
            var Q58;
            Q58=makeQuery(id+"F13.imprint","IMPRINT",FACE,{"disambiguationData":[TD([[makeQuery(id+"F13.imprint","IMPRINT",EDGE,{"derivedFrom":sQuery(id+"F13.wireOp",EDGE,"E30.2.0.7")}),1.0]])]});
            var Q59;
            Q59=makeQuery(id+"F13.imprint","IMPRINT",FACE,{"disambiguationData":[TD([[makeQuery(id+"F13.imprint","IMPRINT",EDGE,{"derivedFrom":sQuery(id+"F13.wireOp",EDGE,"E30.2.0.10")}),1.0]])]});
            var Q60;
            Q60=makeQuery(id+"F13.imprint","IMPRINT",FACE,{"disambiguationData":[TD([[makeQuery(id+"F13.imprint","IMPRINT",EDGE,{"derivedFrom":sQuery(id+"F13.wireOp",EDGE,"E30.2.0.11")}),1.0]])]});
            var Q61;
            Q61=makeQuery(id+"F13.imprint","IMPRINT",FACE,{"disambiguationData":[TD([[makeQuery(id+"F13.imprint","IMPRINT",EDGE,{"derivedFrom":sQuery(id+"F13.wireOp",EDGE,"E30.2.0.12")}),1.0]])]});
            var Q62;
            Q62=makeQuery(id+"F13.imprint","IMPRINT",FACE,{"disambiguationData":[TD([[makeQuery(id+"F13.imprint","IMPRINT",EDGE,{"derivedFrom":sQuery(id+"F13.wireOp",EDGE,"E30.2.0.9")}),1.0]])]});
            var Q63;
            Q63=sQuery(id+"F13.wireOp",EDGE,"E26");
            var Q64;
            Q64=makeQuery(id+"F8.opExtrude","SWEPT_FACE",FACE,{"disambiguationData":[OSD([sQuery(id+"F6.wireOp",EDGE,"E15.right")])]});
            extrude(context, id + "F16", {"entities" : qUnion([Q0, Q1, Q2, Q3, Q4, Q5, Q6, Q7, Q8, Q9, Q10, Q11, Q12, Q13, Q14, Q15, Q16, Q17, Q18, Q19, Q20, Q21, Q22, Q23, Q24, Q25, Q26, Q27, Q28, Q29, Q30, Q31, Q32, Q33, Q34, Q35, Q36, Q37, Q38, Q39, Q40, Q41, Q42, Q43, Q44, Q45, Q46, Q47, Q48, Q49, Q50, Q51, Q52, Q53, Q54, Q55, Q56, Q57, Q58, Q59, Q60, Q61, Q62]), "operationType" : NewBodyOperationType.REMOVE, "surfaceEntities" : qUnion([Q63]), "endBound" : BoundingType.UP_TO_SURFACE, "oppositeDirection" : true, "depth" : 2 * mm, "endBoundEntityFace" : qUnion([Q64]), "offsetDistance" : 25 * mm});
        }
        {
            var Q0;
            Q0=makeQuery(id+"F15.imprint","IMPRINT",FACE,{"disambiguationData":[TD([[makeQuery(id+"F15.imprint","IMPRINT",EDGE,{"derivedFrom":sQuery(id+"F15.wireOp",EDGE,"E37")}),1.0]])]});
            var Q1;
            Q1=makeQuery(id+"F15.imprint","IMPRINT",FACE,{"disambiguationData":[TD([[makeQuery(id+"F15.imprint","IMPRINT",EDGE,{"derivedFrom":sQuery(id+"F15.wireOp",EDGE,"E39")}),1.0]])]});
            var Q2;
            Q2=makeQuery(id+"F15.imprint","IMPRINT",FACE,{"disambiguationData":[TD([[makeQuery(id+"F15.imprint","IMPRINT",EDGE,{"derivedFrom":makeQuery(id+"F9.imprint","IMPRINT",EDGE,{"derivedFrom":sQuery(id+"F9.wireOp",EDGE,"E19.bottom")})}),1.0]])]});
            var Q3;
            Q3=makeQuery(id+"F15.imprint","IMPRINT",FACE,{"disambiguationData":[TD([[makeQuery(id+"F15.imprint","IMPRINT",EDGE,{"derivedFrom":sQuery(id+"F15.wireOp",EDGE,"E40")}),1.0]])]});
            var Q4;
            Q4=makeQuery(id+"F15.imprint","IMPRINT",FACE,{"disambiguationData":[TD([[makeQuery(id+"F15.imprint","IMPRINT",EDGE,{"derivedFrom":sQuery(id+"F15.wireOp",EDGE,"E42.1.0.0")}),1.0]])]});
            var Q5;
            Q5=makeQuery(id+"F15.imprint","IMPRINT",FACE,{"disambiguationData":[TD([[makeQuery(id+"F15.imprint","IMPRINT",EDGE,{"derivedFrom":sQuery(id+"F15.wireOp",EDGE,"E42.1.0.1")}),1.0]])]});
            var Q6;
            Q6=sQuery(id+"F15.wireOp",EDGE,"E39");
            var Q7;
            Q7=makeQuery(id+"F8.opExtrude","SWEPT_FACE",FACE,{"disambiguationData":[OSD([sQuery(id+"F6.wireOp",EDGE,"E15.left")])]});
            extrude(context, id + "F17", {"entities" : qUnion([Q0, Q1, Q2, Q3, Q4, Q5]), "operationType" : NewBodyOperationType.REMOVE, "surfaceEntities" : qUnion([Q6]), "endBound" : BoundingType.UP_TO_SURFACE, "oppositeDirection" : true, "depth" : 2 * mm, "endBoundEntityFace" : qUnion([Q7]), "offsetDistance" : 25 * mm});
        }
        {
            var Q0;
            {var subQ0=sQuery(id+"F6.wireOp",EDGE,"E16.right");var subQ1=sQuery(id+"F6.wireOp",EDGE,"E16.top");Q0=makeQuery(id+"F8.boolean.opBoolean","MERGE",EDGE,{"derivedFrom":[makeQuery(id+"F7.opExtrude","SWEPT_EDGE",EDGE,{"disambiguationData":[OSD([subQ1,subQ0])]}),makeQuery(id+"F8.opExtrude","SWEPT_EDGE",EDGE,{"disambiguationData":[OSD([subQ1,subQ0])]})]});}
            var Q1;
            Q1=makeQuery(id+"F8.opExtrude","SWEPT_EDGE",EDGE,{"disambiguationData":[OSD([sQuery(id+"F6.wireOp",EDGE,"E15.top"),sQuery(id+"F6.wireOp",EDGE,"E15.right")])]});
            var Q2;
            Q2=makeQuery(id+"F8.opExtrude","SWEPT_EDGE",EDGE,{"disambiguationData":[OSD([sQuery(id+"F6.wireOp",EDGE,"E15.bottom"),sQuery(id+"F6.wireOp",EDGE,"E15.right")])]});
            var Q3;
            {var subQ0=sQuery(id+"F6.wireOp",EDGE,"E16.right");var subQ1=sQuery(id+"F6.wireOp",EDGE,"E16.bottom");Q3=makeQuery(id+"F8.boolean.opBoolean","MERGE",EDGE,{"derivedFrom":[makeQuery(id+"F7.opExtrude","SWEPT_EDGE",EDGE,{"disambiguationData":[OSD([subQ1,subQ0])]}),makeQuery(id+"F8.opExtrude","SWEPT_EDGE",EDGE,{"disambiguationData":[OSD([subQ1,subQ0])]})]});}
            var Q4;
            {var subQ0=sQuery(id+"F6.wireOp",EDGE,"E16.left");var subQ1=sQuery(id+"F6.wireOp",EDGE,"E16.bottom");Q4=makeQuery(id+"F8.boolean.opBoolean","MERGE",EDGE,{"derivedFrom":[makeQuery(id+"F7.opExtrude","SWEPT_EDGE",EDGE,{"disambiguationData":[OSD([subQ1,subQ0])]}),makeQuery(id+"F8.opExtrude","SWEPT_EDGE",EDGE,{"disambiguationData":[OSD([subQ1,subQ0])]})]});}
            var Q5;
            Q5=makeQuery(id+"F8.opExtrude","SWEPT_EDGE",EDGE,{"disambiguationData":[OSD([sQuery(id+"F6.wireOp",EDGE,"E15.bottom"),sQuery(id+"F6.wireOp",EDGE,"E15.left")])]});
            var Q6;
            {var subQ0=sQuery(id+"F6.wireOp",EDGE,"E16.left");var subQ1=sQuery(id+"F6.wireOp",EDGE,"E16.top");Q6=makeQuery(id+"F8.boolean.opBoolean","MERGE",EDGE,{"derivedFrom":[makeQuery(id+"F7.opExtrude","SWEPT_EDGE",EDGE,{"disambiguationData":[OSD([subQ1,subQ0])]}),makeQuery(id+"F8.opExtrude","SWEPT_EDGE",EDGE,{"disambiguationData":[OSD([subQ1,subQ0])]})]});}
            var Q7;
            Q7=makeQuery(id+"F8.opExtrude","SWEPT_EDGE",EDGE,{"disambiguationData":[OSD([sQuery(id+"F6.wireOp",EDGE,"E15.top"),sQuery(id+"F6.wireOp",EDGE,"E15.left")])]});
            fillet(context, id + "F18", {"entities" : qUnion([Q0, Q1, Q2, Q3, Q4, Q5, Q6, Q7]), "radius" : 5 * mm, "tangentPropagation" : true, "allowEdgeOverflow" : false});
        }
        {
            var Q0;
            Q0=makeQuery(id+"F13.imprint","IMPRINT",FACE,{"disambiguationData":[TD([[makeQuery(id+"F13.imprint","IMPRINT",EDGE,{"derivedFrom":sQuery(id+"F13.wireOp",EDGE,"E32")}),1.0]])]});
            var Q1;
            Q1=makeQuery(id+"F13.imprint","IMPRINT",FACE,{"disambiguationData":[TD([[makeQuery(id+"F13.imprint","IMPRINT",EDGE,{"derivedFrom":sQuery(id+"F13.wireOp",EDGE,"E33")}),1.0]])]});
            extrude(context, id + "F19", {"entities" : qUnion([Q0, Q1]), "operationType" : NewBodyOperationType.REMOVE, "oppositeDirection" : true, "depth" : 2 * mm, "offsetDistance" : 25 * mm});
        }
        {
            var Q0;
            Q0=makeQuery(id+"F8.opExtrude","CAP_FACE",FACE,{"disambiguationData":[OSD([sQuery(id+"F6.wireOp",EDGE,"E15.bottom"),sQuery(id+"F6.wireOp",EDGE,"E15.top"),sQuery(id+"F6.wireOp",EDGE,"E15.left"),sQuery(id+"F6.wireOp",EDGE,"E15.right"),sQuery(id+"F6.wireOp",EDGE,"E16.bottom"),sQuery(id+"F6.wireOp",EDGE,"E16.top"),sQuery(id+"F6.wireOp",EDGE,"E16.left"),sQuery(id+"F6.wireOp",EDGE,"E16.right")])],"isStart":false});
            var sketch = newSketch(context, id + "F20", { "sketchPlane" : qUnion([Q0])});
            skLineSegment(sketch, "E46.bottom", {"start": v(-53.5, 49.5) * mm, "end": v(53.5, 49.5) * mm});
            skLineSegment(sketch, "E46.top", {"start": v(-53.5, -49.5) * mm, "end": v(53.5, -49.5) * mm});
            skLineSegment(sketch, "E46.left", {"start": v(-58.5, 44.5) * mm, "end": v(-58.5, -44.5) * mm});
            skLineSegment(sketch, "E46.right", {"start": v(58.5, 44.5) * mm, "end": v(58.5, -44.5) * mm});
            skPoint(sketch, "E47.visualSharp", {"position": v(-58.5, 49.5) * mm});
            skArc(sketch, "E47.filletArc", {"start": v(-53.5, 49.5) * mm, "mid": v(-57.04, 48.04) * mm, "end": v(-58.5, 44.5) * mm});
            skPoint(sketch, "E48.visualSharp", {"position": v(58.5, 49.5) * mm});
            skArc(sketch, "E48.filletArc", {"start": v(58.5, 44.5) * mm, "mid": v(57.04, 48.04) * mm, "end": v(53.5, 49.5) * mm});
            skPoint(sketch, "E49.visualSharp", {"position": v(58.5, -49.5) * mm});
            skArc(sketch, "E49.filletArc", {"start": v(53.5, -49.5) * mm, "mid": v(57.04, -48.04) * mm, "end": v(58.5, -44.5) * mm});
            skPoint(sketch, "E50.visualSharp", {"position": v(-58.5, -49.5) * mm});
            skArc(sketch, "E50.filletArc", {"start": v(-58.5, -44.5) * mm, "mid": v(-57.04, -48.04) * mm, "end": v(-53.5, -49.5) * mm});
            skCircle(sketch, "E51", {"center": v(-53.5, 44.5) * mm, "radius": 5.04 * mm});
            skCircle(sketch, "E52", {"center": v(-53.5, 44.5) * mm, "radius": 1.4 * mm});
            skCircle(sketch, "E53", {"center": v(53.5, 44.5) * mm, "radius": 5.04 * mm});
            skCircle(sketch, "E54", {"center": v(53.5, 44.5) * mm, "radius": 1.4 * mm});
            skCircle(sketch, "E55", {"center": v(53.5, -44.5) * mm, "radius": 5.04 * mm});
            skCircle(sketch, "E56", {"center": v(53.5, -44.5) * mm, "radius": 1.4 * mm});
            skCircle(sketch, "E57", {"center": v(-53.5, -44.5) * mm, "radius": 5.04 * mm});
            skCircle(sketch, "E58", {"center": v(-53.5, -44.5) * mm, "radius": 1.4 * mm});
            skSolve(sketch);
        }
        {
            var Q0;
            Q0=makeQuery(id+"F20.imprint","IMPRINT",FACE,{"disambiguationData":[TD([[makeQuery(id+"F20.imprint","IMPRINT",EDGE,{"derivedFrom":sQuery(id+"F20.wireOp",EDGE,"E52")}),-1.0]])]});
            var Q1;
            Q1=makeQuery(id+"F20.imprint","IMPRINT",FACE,{"disambiguationData":[TD([[makeQuery(id+"F20.imprint","IMPRINT",EDGE,{"derivedFrom":sQuery(id+"F20.wireOp",EDGE,"E54")}),-1.0]])]});
            var Q2;
            Q2=makeQuery(id+"F20.imprint","IMPRINT",FACE,{"disambiguationData":[TD([[makeQuery(id+"F20.imprint","IMPRINT",EDGE,{"derivedFrom":sQuery(id+"F20.wireOp",EDGE,"E56")}),-1.0]])]});
            var Q3;
            Q3=makeQuery(id+"F20.imprint","IMPRINT",FACE,{"disambiguationData":[TD([[makeQuery(id+"F20.imprint","IMPRINT",EDGE,{"derivedFrom":sQuery(id+"F20.wireOp",EDGE,"E58")}),-1.0]])]});
            var Q4;
            Q4=sQuery(id+"F20.wireOp",EDGE,"E51");
            var Q5;
            Q5=sQuery(id+"F20.wireOp",EDGE,"E52");
            extrude(context, id + "F21", {"entities" : qUnion([Q0, Q1, Q2, Q3]), "operationType" : NewBodyOperationType.ADD, "surfaceEntities" : qUnion([Q4, Q5]), "oppositeDirection" : true, "depth" : 6 * mm, "offsetDistance" : 25 * mm});
        }
        {
            var Q0;
            Q0=makeQuery(id+"F21.opExtrude","CAP_EDGE",EDGE,{"disambiguationData":[OSD([sQuery(id+"F20.wireOp",EDGE,"E51")])],"isStart":false});
            var Q1;
            Q1=makeQuery(id+"F21.opExtrude","CAP_EDGE",EDGE,{"disambiguationData":[OSD([sQuery(id+"F20.wireOp",EDGE,"E53")])],"isStart":false});
            var Q2;
            Q2=makeQuery(id+"F21.opExtrude","CAP_EDGE",EDGE,{"disambiguationData":[OSD([sQuery(id+"F20.wireOp",EDGE,"E55")])],"isStart":false});
            var Q3;
            Q3=makeQuery(id+"F21.opExtrude","CAP_EDGE",EDGE,{"disambiguationData":[OSD([sQuery(id+"F20.wireOp",EDGE,"E57")])],"isStart":false});
            chamfer(context, id + "F22", {"entities" : qUnion([Q0, Q1, Q2, Q3]), "chamferType" : ChamferType.OFFSET_ANGLE, "width" : 6 * mm, "oppositeDirection" : false, "angle" : 22.5 * degree});
        }
        {
            var Q0;
            {var subQ0=sQuery(id+"F20.wireOp",EDGE,"E51");var subQ1=sQuery(id+"F20.wireOp",EDGE,"E46.bottom");var subQ2=makeQuery(id+"F20.imprint","INTERSECT",VERTEX,{"derivedFrom":[subQ1,subQ0]});Q0=makeQuery(id+"F20.imprint","IMPRINT",FACE,{"disambiguationData":[TD([[makeQuery(id+"F20.imprint","IMPRINT",EDGE,{"disambiguationData":[TD([[subQ2,-1.0]])],"derivedFrom":subQ1}),-1.0]])]});}
            var sketch = newSketch(context, id + "F23", { "sketchPlane" : qUnion([Q0])});
            skLineSegment(sketch, "E59.bottom", {"start": v(-53.5, 49.5) * mm, "end": v(53.5, 49.5) * mm});
            skLineSegment(sketch, "E59.top", {"start": v(-53.5, -49.5) * mm, "end": v(53.5, -49.5) * mm});
            skLineSegment(sketch, "E59.left", {"start": v(-58.5, 44.5) * mm, "end": v(-58.5, -44.5) * mm});
            skLineSegment(sketch, "E59.right", {"start": v(58.5, 44.5) * mm, "end": v(58.5, -44.5) * mm});
            skPoint(sketch, "E60.visualSharp", {"position": v(-58.5, 49.5) * mm});
            skArc(sketch, "E60.filletArc", {"start": v(-53.5, 49.5) * mm, "mid": v(-57.04, 48.04) * mm, "end": v(-58.5, 44.5) * mm});
            skPoint(sketch, "E61.visualSharp", {"position": v(58.5, 49.5) * mm});
            skArc(sketch, "E61.filletArc", {"start": v(58.5, 44.5) * mm, "mid": v(57.04, 48.04) * mm, "end": v(53.5, 49.5) * mm});
            skPoint(sketch, "E62.visualSharp", {"position": v(58.5, -49.5) * mm});
            skArc(sketch, "E62.filletArc", {"start": v(53.5, -49.5) * mm, "mid": v(57.04, -48.04) * mm, "end": v(58.5, -44.5) * mm});
            skPoint(sketch, "E63.visualSharp", {"position": v(-58.5, -49.5) * mm});
            skArc(sketch, "E63.filletArc", {"start": v(-58.5, -44.5) * mm, "mid": v(-57.04, -48.04) * mm, "end": v(-53.5, -49.5) * mm});
            skCircle(sketch, "E64", {"center": v(-53.5, 44.5) * mm, "radius": 1.4 * mm});
            skCircle(sketch, "E65", {"center": v(53.5, 44.5) * mm, "radius": 1.4 * mm});
            skCircle(sketch, "E66", {"center": v(-53.5, -44.5) * mm, "radius": 1.4 * mm});
            skCircle(sketch, "E67", {"center": v(53.5, -44.5) * mm, "radius": 1.4 * mm});
            skSolve(sketch);
        }
        {
            var Q0;
            Q0 = qSketchRegion(id + "F23", true);
            extrude(context, id + "F24", {"entities" : qUnion([Q0]), "depth" : 2 * mm, "offsetDistance" : 25 * mm});
        }
        {
            var Q0;
            Q0=makeQuery(id+"F0.imprint","IMPRINT",FACE,{"disambiguationData":[TD([[makeQuery(id+"F0.imprint","IMPRINT",EDGE,{"derivedFrom":sQuery(id+"F0.wireOp",EDGE,"E8.bottom")}),1.0]])]});
            extrude(context, id + "F25", {"entities" : qUnion([Q0]), "operationType" : NewBodyOperationType.ADD, "depth" : 20 * mm, "offsetDistance" : 25 * mm});
        }
        {
            var Q0;
            Q0=makeQuery(id+"F0.imprint","IMPRINT",FACE,{"disambiguationData":[TD([[makeQuery(id+"F0.imprint","IMPRINT",EDGE,{"derivedFrom":sQuery(id+"F0.wireOp",EDGE,"E10.bottom")}),-1.0]])]});
            var Q1;
            Q1=makeQuery(id+"F0.imprint","IMPRINT",FACE,{"disambiguationData":[TD([[makeQuery(id+"F0.imprint","IMPRINT",EDGE,{"derivedFrom":sQuery(id+"F0.wireOp",EDGE,"E9.bottom")}),-1.0]])]});
            extrude(context, id + "F26", {"entities" : qUnion([Q0, Q1]), "depth" : 9 * mm, "offsetDistance" : 25 * mm});
        }
    });
